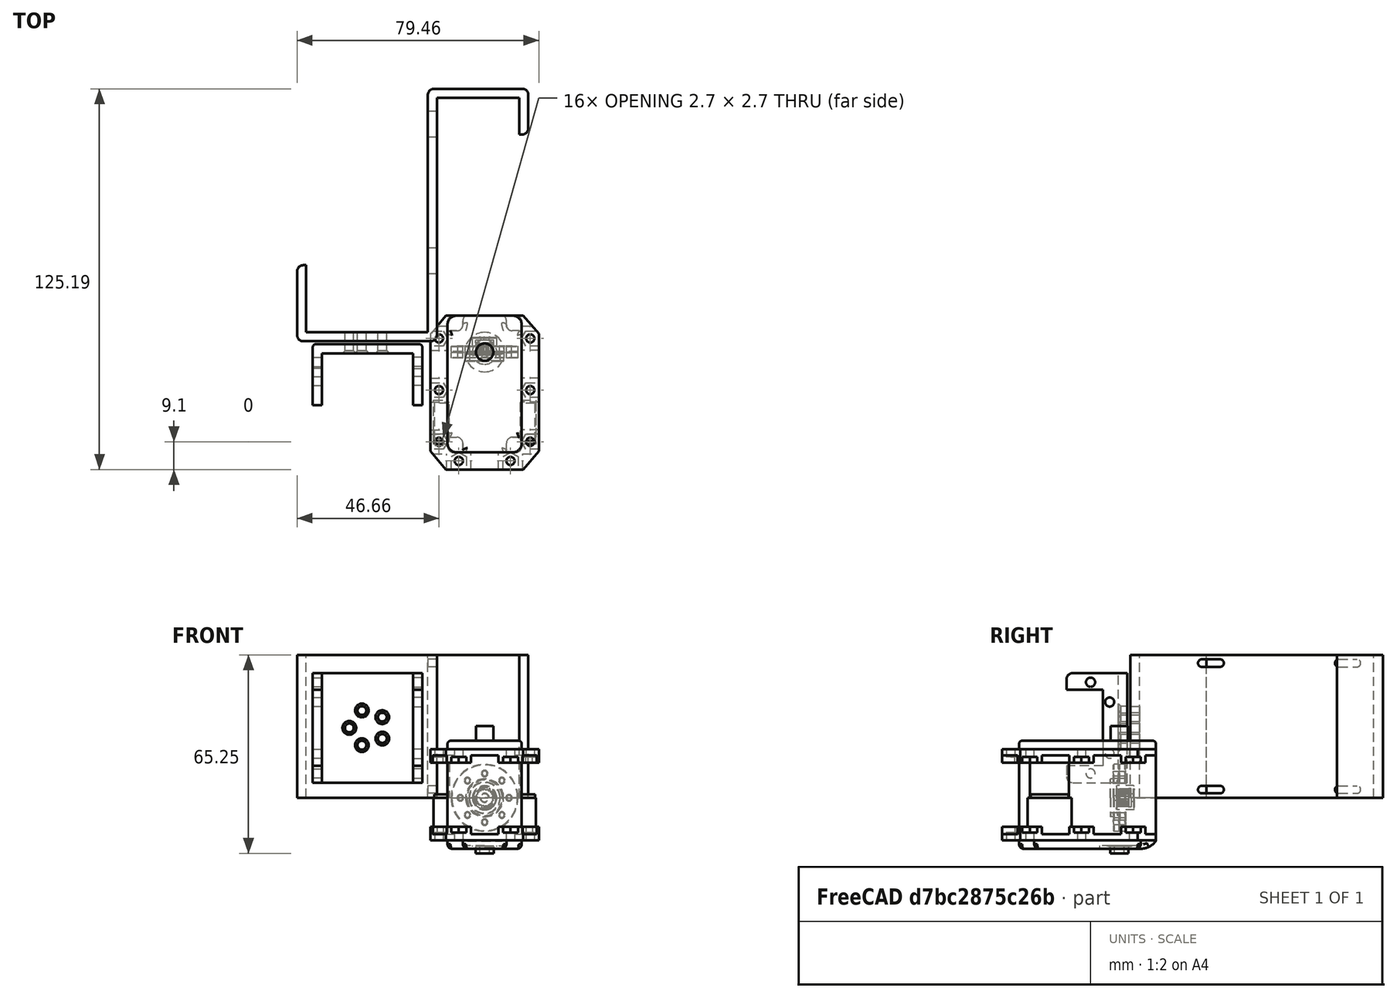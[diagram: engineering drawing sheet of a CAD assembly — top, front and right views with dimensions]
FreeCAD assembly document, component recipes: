
FREECAD ASSEMBLY — COMPONENT RECIPES ("test2")

This assembly document has 7 components, labeled P0..P6 below (a component is one placed body or linked part). 4 of them carry a construction recipe — the FreeCAD feature program that regenerates the part from scratch, quoted from this document or its linked companion documents; the rest are supplied as boundary geometry only. No exploded tour is included for this assembly.
COMPONENT P0 — geometry summary ("ASM0001_ASM"; no construction recipe available for this part):
  bounding box: 50.9 x 40.0 x 33.5 mm
  tessellated surface: 109,530 triangles
  volume: 42792 mm^3 (63% of its bounding box)
COMPONENT P1 — geometry summary ("ASM0001_ASM001"; no construction recipe available for this part):
  bounding box: 50.9 x 40.0 x 33.5 mm
  tessellated surface: 109,530 triangles
  volume: 42792 mm^3 (63% of its bounding box)
COMPONENT P2 — recipe-attached ("Body003", modeled in this document).
Construction recipe (the document's own serialized feature program — sketch geometry with constraints, then the solid features built on it; lengths are millimeters unless a unit is written):

FEATURE [PartDesign::ShapeBinder] CopyPart__Feature
  TraceSupport = false
FEATURE [Sketcher::SketchObject] Sketch002
  ArcFitTolerance = 1e-06
  AttachmentSupport = -> [CopyPart__Feature]
  ExternalTypes = [0]
  FullyConstrained = true
  MakeInternals = false
  MapMode = 5
  Placement = pos=(0,-38.6,0) rot=(1,0,0;1.5708rad)
  _ExternalGeoVersion = 1
  sketch-geometry (5):
    g0: LineSegment StartX=-18 StartY=-15 StartZ=0 EndX=18 EndY=-15 EndZ=0
    g1: LineSegment StartX=18 StartY=-15 StartZ=0 EndX=18 EndY=15 EndZ=0
    g2: LineSegment StartX=18 StartY=15 StartZ=0 EndX=-18 EndY=15 EndZ=0
    g3: LineSegment StartX=-18 StartY=15 StartZ=0 EndX=-18 EndY=-15 EndZ=0
    g4: GeomPoint [constr] X=0 Y=0 Z=0
  constraints (12):
    c: Coincident(g0,g1)
    c: Coincident(g1,g2)
    c: Coincident(g2,g3)
    c: Coincident(g3,g0)
    c: Horizontal(g0)
    c: Horizontal(g2)
    c: Vertical(g1)
    c: Vertical(g3)
    c: Symmetric(g2,g0,g4)
    c: Distance(g1,g3) = 36
    c: Distance(g0,g2) = 30
    c: Coincident(g4,g-1)
FEATURE [PartDesign::Pad] Pad001
  Direction = (0,-1,2e-16)
  Length = 3
  Length2 = 10
  Profile = -> Sketch002
  ReferenceAxis = -> Sketch002 [N_Axis]
  Refine = true
  SideType = 0
  Suppressed = false
  Type = 0
  Type2 = 0
FEATURE [Sketcher::SketchObject] Sketch003
  ArcFitTolerance = 1e-06
  AttachmentSupport = -> [Pad001]
  ExternalTypes = [0]
  FullyConstrained = true
  MakeInternals = false
  MapMode = 5
  Placement = pos=(0,3.3e-15,15) rot=(0,0,1;0rad)
  _ExternalGeoVersion = 1
  sketch-geometry (12):
    g0: LineSegment StartX=-18 StartY=-21.6 StartZ=0 EndX=-12.5 EndY=-21.6 EndZ=0
    g1: LineSegment StartX=-12.5 StartY=-21.6 StartZ=0 EndX=-12.5 EndY=-33.6 EndZ=0
    g2: LineSegment StartX=-12.5 StartY=-33.6 StartZ=0 EndX=12.5 EndY=-33.6 EndZ=0
    g3: LineSegment StartX=12.5 StartY=-33.6 StartZ=0 EndX=12.5 EndY=-21.6 EndZ=0
    g4: LineSegment StartX=12.5 StartY=-21.6 StartZ=0 EndX=18 EndY=-21.6 EndZ=0
    g5: LineSegment StartX=18 StartY=-21.6 StartZ=0 EndX=18 EndY=-41.6 EndZ=0
    g6: LineSegment StartX=18 StartY=-41.6 StartZ=0 EndX=-18 EndY=-41.6 EndZ=0
    g7: LineSegment StartX=-18 StartY=-41.6 StartZ=0 EndX=-18 EndY=-21.6 EndZ=0
    g8: Circle CenterX=-15 CenterY=-29.5 CenterZ=0 NormalX=0 NormalY=0 NormalZ=1 AngleXU=0 Radius=1.5
    g9: Circle CenterX=-8.5 CenterY=-35.8 CenterZ=0 NormalX=0 NormalY=0 NormalZ=1 AngleXU=0 Radius=1.5
    g10: Circle CenterX=8.5 CenterY=-35.8 CenterZ=0 NormalX=0 NormalY=0 NormalZ=1 AngleXU=0 Radius=1.5
    g11: Circle CenterX=15 CenterY=-29.5 CenterZ=0 NormalX=0 NormalY=0 NormalZ=1 AngleXU=0 Radius=1.5
  constraints (36):
    c: Horizontal(g0)
    c: Coincident(g0,g1)
    c: Vertical(g1)
    c: Coincident(g1,g2)
    c: Horizontal(g2)
    c: Coincident(g2,g3)
    c: Vertical(g3)
    c: Coincident(g3,g4)
    c: Horizontal(g4)
    c: Coincident(g4,g5)
    c: Vertical(g5)
    c: Coincident(g5,g6)
    c: Horizontal(g6)
    c: Coincident(g6,g7)
    c: Coincident(g7,g0)
    c: Vertical(g7)
    c: DistanceX(g6,g6) = 36
    c: DistanceY(g7,g7) = 20
    c: Distance(g3,g1) = 25
    c: Equal(g0,g4)
    c: Equal(g3,g1)
    c: Distance(g-1,g6) = 41.6
    c: Distance(g-2,g7) = 18
    c: Distance(g6,g2) = 8
    c: Diameter(g8) = 3
    c: Equal(g8,g9)
    c: Equal(g9,g10)
    c: Equal(g10,g11)
    c: Distance(g8,g7) = 3
    c: Distance(g9,g6) = 5.8
    c: Distance(g9,g7) = 9.5
    c: Distance(g10,g5) = 9.5
    c: Distance(g10,g6) = 5.8
    c: Distance(g11,g5) = 3
    c: Distance(g8,g0) = 7.9
    c: Distance(g11,g4) = 7.9
FEATURE [PartDesign::Pad] Pad002
  BaseFeature = -> Pad001
  Direction = (0,0,1)
  Length = 3
  Length2 = 10
  Profile = -> Sketch003
  ReferenceAxis = -> Sketch003 [N_Axis]
  Refine = true
  SideType = 0
  Suppressed = false
  Type = 0
  Type2 = 0
FEATURE [PartDesign::Mirrored] Mirrored
  BaseFeature = -> Pad002
  MirrorPlane = -> XY_Plane001
  Originals = -> [Pad002]
  Refine = true
  Suppressed = false
  TransformMode = 0
FEATURE [PartDesign::Fillet] Fillet001
  Base = -> Mirrored [Edge60,Edge47,Edge36,Edge27]
  BaseFeature = -> Mirrored
  Radius = 2
  Refine = true
  SupportTransform = false
  Suppressed = false
  UseAllEdges = false
FEATURE [PartDesign::Fillet] Fillet002
  Base = -> Fillet001 [Edge51,Edge56]
  BaseFeature = -> Fillet001
  Radius = 1
  Refine = true
  SupportTransform = false
  Suppressed = false
  UseAllEdges = false
FEATURE [Sketcher::SketchObject] Sketch004
  ArcFitTolerance = 1e-06
  AttachmentSupport = -> [Fillet002]
  ExternalTypes = [0]
  FullyConstrained = true
  MakeInternals = false
  MapMode = 5
  Placement = pos=(0,-38.6,0) rot=(0,0.707107,0.707107;3.14159rad)
  _ExternalGeoVersion = 1
  sketch-geometry (1):
    g0: Circle CenterX=0 CenterY=6 CenterZ=0 NormalX=0 NormalY=0 NormalZ=1 AngleXU=0 Radius=1.25
  constraints (3):
    c: Diameter(g0) = 2.5
    c: PointOnObject(g0,g-2)
    c: Distance(g0,g-1) = 6
FEATURE [PartDesign::Hole] Hole
  BaseFeature = -> Fillet002
  BaseProfileType = 7
  CustomThreadClearance = 0
  Depth = 5
  DepthType = 0
  Diameter = 2.9
  DrillForDepth = false
  DrillPoint = 1
  DrillPointAngle = 118
  HoleCutCountersinkAngle = 90
  HoleCutCustomValues = false
  HoleCutDepth = 2.65
  HoleCutDiameter = 5.3
  HoleCutType = 7
  ModelThread = false
  Profile = -> Sketch004
  Refine = true
  Suppressed = false
  Tapered = false
  TaperedAngle = 90
  ThreadClass = 0
  ThreadDepth = 5
  ThreadDepthType = 0
  ThreadDiameter = 2.5
  ThreadDirection = 0
  ThreadFit = 0
  ThreadSize = 8
  ThreadType = 1
  Threaded = false
  UseCustomThreadClearance = false
FEATURE [PartDesign::PolarPattern] PolarPattern
  Angle = 360
  Axis = -> Sketch004 [N_Axis]
  BaseFeature = -> Hole
  Mode = 0
  Occurrences = 5
  Offset = 120
  Originals = -> [Hole]
  Refine = true
  SpacingPattern = [0]
  Spacings = [-1,-1,-1,-1]
  Suppressed = false
  TransformMode = 0
FEATURE [PartDesign::Body] Body001
  AllowCompound = true
  Group = -> [CopyPart__Feature,Sketch002,Pad001,Sketch003,Pad002,Mirrored,Fillet001,Fillet002,Sketch004,Hole,PolarPattern]
  Origin = -> Origin002
  Placement = pos=(-38.5,-39,23) rot=(0.707107,0,-0.707107;3.14159rad)
  Tip = -> PolarPattern
COMPONENT P3 — recipe-attached ("Body004", modeled in this document).
Construction recipe (the document's own serialized feature program — sketch geometry with constraints, then the solid features built on it; lengths are millimeters unless a unit is written):

FEATURE [Sketcher::SketchObject] Sketch
  ArcFitTolerance = 1e-06
  AttachmentSupport = -> [Origin]
  ExternalTypes = [0]
  FullyConstrained = true
  MakeInternals = false
  MapMode = 5
  _ExternalGeoVersion = 1
  sketch-geometry (12):
    g0: LineSegment StartX=-18.66 StartY=86.59 StartZ=0 EndX=-18.66 EndY=6.59 EndZ=0
    g1: LineSegment StartX=-61.66 StartY=3.59 StartZ=0 EndX=-61.66 EndY=28.59 EndZ=0
    g2: LineSegment StartX=-61.66 StartY=28.59 StartZ=0 EndX=-58.66 EndY=28.59 EndZ=0
    g3: LineSegment StartX=-58.66 StartY=28.59 StartZ=0 EndX=-58.66 EndY=6.59 EndZ=0
    g4: LineSegment StartX=-58.66 StartY=6.59 StartZ=0 EndX=-18.66 EndY=6.59 EndZ=0
    g5: LineSegment StartX=-15.66 StartY=83.59 StartZ=0 EndX=-15.66 EndY=3.59 EndZ=0
    g6: LineSegment StartX=-15.66 StartY=3.59 StartZ=0 EndX=-61.66 EndY=3.59 EndZ=0
    g7: LineSegment StartX=-15.66 StartY=83.59 StartZ=0 EndX=11.34 EndY=83.59 EndZ=0
    g8: LineSegment StartX=11.34 StartY=83.59 StartZ=0 EndX=11.34 EndY=71.59 EndZ=0
    g9: LineSegment StartX=11.34 StartY=71.59 StartZ=0 EndX=14.34 EndY=71.59 EndZ=0
    g10: LineSegment StartX=14.34 StartY=71.59 StartZ=0 EndX=14.34 EndY=86.59 EndZ=0
    g11: LineSegment StartX=14.34 StartY=86.59 StartZ=0 EndX=-18.66 EndY=86.59 EndZ=0
  constraints (36):
    c: Coincident(g1,g2)
    c: Coincident(g2,g3)
    c: Coincident(g3,g4)
    c: Coincident(g4,g0)
    c: Distance(g2,g2) = 3
    c: Vertical(g5)
    c: Coincident(g5,g6)
    c: Coincident(g6,g1)
    c: Perpendicular(g4,g3)
    c: Horizontal(g4)
    c: Horizontal(g6)
    c: Vertical(g1)
    c: Vertical(g0)
    c: Horizontal(g2)
    c: Distance(g6,g4) = 3
    c: Distance(g5,g0) = 3
    c: DistanceX(g4,g4) = 40
    c: Distance(g1,g1) = 25
    c: Distance(g-2,g5) = 15.66
    c: Distance(g-1,g6) = 3.59
    c: DistanceY(g0,g0) = 80
    c: Coincident(g5,g7)
    c: Horizontal(g7)
    c: Coincident(g7,g8)
    c: Vertical(g8)
    c: Coincident(g8,g9)
    c: Horizontal(g9)
    c: Coincident(g9,g10)
    c: Vertical(g10)
    c: Coincident(g10,g11)
    c: Coincident(g11,g0)
    c: Equal(g9,g2)
    c: Horizontal(g11)
    c: Distance(g11,g7) = 3
    c: Distance(g7,g7) = 27
    c: DistanceY(g10,g10) = 15
FEATURE [PartDesign::Pad] Pad
  Direction = (0,0,1)
  Length = 47
  Length2 = 10
  Profile = -> Sketch
  ReferenceAxis = -> Sketch [N_Axis]
  Refine = true
  SideType = 0
  Suppressed = false
  Type = 0
  Type2 = 0
FEATURE [Sketcher::SketchObject] Sketch001
  ArcFitTolerance = 1e-06
  ExternalTypes = [0]
  FullyConstrained = true
  MakeInternals = false
  MapMode = 5
  Placement = pos=(-15.66,0,0) rot=(0.57735,0.57735,0.57735;2.0944rad)
  _ExternalGeoVersion = 1
  sketch-geometry (8):
    g0: ArcOfCircle CenterX=72.09 CenterY=2.7 CenterZ=0 NormalX=0 NormalY=0 NormalZ=1 AngleXU=0 Radius=1.25 StartAngle=1.5708 EndAngle=4.71239
    g1: ArcOfCircle CenterX=78.09 CenterY=2.7 CenterZ=0 NormalX=0 NormalY=0 NormalZ=1 AngleXU=0 Radius=1.25 StartAngle=4.71239 EndAngle=7.85398
    g2: LineSegment StartX=72.09 StartY=3.95 StartZ=0 EndX=78.09 EndY=3.95 EndZ=0
    g3: LineSegment StartX=72.09 StartY=1.45 StartZ=0 EndX=78.09 EndY=1.45 EndZ=0
    g4: ArcOfCircle CenterX=27.09 CenterY=2.7 CenterZ=0 NormalX=0 NormalY=0 NormalZ=1 AngleXU=0 Radius=1.25 StartAngle=1.5708 EndAngle=4.71239
    g5: ArcOfCircle CenterX=33.09 CenterY=2.7 CenterZ=0 NormalX=0 NormalY=0 NormalZ=1 AngleXU=0 Radius=1.25 StartAngle=4.71239 EndAngle=7.85398
    g6: LineSegment StartX=27.09 StartY=3.95 StartZ=0 EndX=33.09 EndY=3.95 EndZ=0
    g7: LineSegment StartX=27.09 StartY=1.45 StartZ=0 EndX=33.09 EndY=1.45 EndZ=0
  constraints (20):
    c: Tangent(g0,g2) = 1.5708
    c: Tangent(g0,g3) = -1.5708
    c: Tangent(g1,g2) = 1.5708
    c: Tangent(g1,g3) = -1.5708
    c: Equal(g0,g1)
    c: Distance(g0,g1) = 6
    c: Radius(g0) = 1.25
    c: Horizontal(g2)
    c: Distance(g1,g-1) = 2.7
    c: DistanceX(g-1,g1) = 78.09
    c: Tangent(g4,g6) = 1.5708
    c: Tangent(g4,g7) = -1.5708
    c: Tangent(g5,g6) = 1.5708
    c: Tangent(g5,g7) = -1.5708
    c: Equal(g4,g5)
    c: Distance(g4,g5) = 6
    c: Radius(g4) = 1.25
    c: Horizontal(g6)
    c: DistanceX(g5,g1) = 45
    c: Distance(g5,g-1) = 2.7
FEATURE [PartDesign::Fillet] Fillet
  Base = -> Pad [Edge26,Edge29,Edge32,Edge8,Edge11,Edge14]
  BaseFeature = -> Pad
  Radius = 2
  Refine = true
  SupportTransform = false
  Suppressed = false
  UseAllEdges = false
FEATURE [PartDesign::Pocket] Pocket
  BaseFeature = -> Fillet
  Direction = (-1,0,0)
  Length = 5
  Length2 = 5
  Profile = -> Sketch001
  ReferenceAxis = -> Sketch001 [N_Axis]
  Refine = true
  SideType = 0
  Suppressed = false
  Type = 0
  Type2 = 0
FEATURE [PartDesign::LinearPattern] LinearPattern
  BaseFeature = -> Pocket
  Direction = -> Sketch001 [V_Axis]
  Direction2 = -> Sketch001 [V_Axis]
  Length = 41.6
  Length2 = 100
  Mode = 0
  Mode2 = 0
  Occurrences = 2
  Occurrences2 = 1
  Offset = 41.6
  Offset2 = 100
  Originals = -> [Pocket]
  Refine = true
  Reversed2 = false
  SpacingPattern = [0]
  SpacingPattern2 = [0]
  Spacings = [-1]
  Suppressed = false
  TransformMode = 0
FEATURE [Sketcher::SketchObject] Sketch005
  ArcFitTolerance = 1e-06
  AttachmentSupport = -> [LinearPattern]
  ExternalTypes = [0]
  FullyConstrained = true
  MakeInternals = false
  Placement = pos=(0,3.59,0) rot=(1,0,0;1.5708rad)
  _ExternalGeoVersion = 1
  sketch-geometry (5):
    g0: Circle CenterX=-40.37 CenterY=17.3 CenterZ=0 NormalX=0 NormalY=0 NormalZ=1 AngleXU=0 Radius=1.25
    g1: Circle CenterX=-44.5 CenterY=23 CenterZ=0 NormalX=0 NormalY=0 NormalZ=1 AngleXU=0 Radius=1.25
    g2: Circle CenterX=-40.36 CenterY=28.7 CenterZ=0 NormalX=0 NormalY=0 NormalZ=1 AngleXU=0 Radius=1.25
    g3: Circle CenterX=-33.65 CenterY=26.55 CenterZ=0 NormalX=0 NormalY=0 NormalZ=1 AngleXU=0 Radius=1.25
    g4: Circle CenterX=-33.65 CenterY=19.5 CenterZ=0 NormalX=0 NormalY=0 NormalZ=1 AngleXU=0 Radius=1.25
  constraints (15):
    c: Diameter(g0) = 2.5
    c: Distance(g0,g-1) = 17.3
    c: Distance(g0,g-2) = 40.37
    c: Equal(g1,g0)
    c: Distance(g1,g-1) = 23
    c: DistanceX(g1,g-1) = 44.5
    c: Equal(g2,g1)
    c: Equal(g3,g2)
    c: Equal(g4,g3)
    c: Distance(g2,g-1) = 28.7
    c: Distance(g2,g-2) = 40.36
    c: Distance(g3,g-2) = 33.65
    c: Distance(g3,g-1) = 26.55
    c: Distance(g4,g-2) = 33.65
    c: DistanceY(g-1,g4) = 19.5
FEATURE [PartDesign::Hole] Hole001
  BaseFeature = -> LinearPattern
  BaseProfileType = 7
  CustomThreadClearance = 0
  Depth = 5
  DepthType = 0
  Diameter = 2.9
  DrillForDepth = false
  DrillPoint = 1
  DrillPointAngle = 118
  HoleCutCountersinkAngle = 90
  HoleCutCustomValues = false
  HoleCutDepth = 0
  HoleCutDiameter = 5.3
  HoleCutType = 0
  ModelThread = false
  Profile = -> Sketch005
  Refine = true
  Suppressed = false
  Tapered = false
  TaperedAngle = 90
  ThreadClass = 0
  ThreadDepth = 5
  ThreadDepthType = 0
  ThreadDiameter = 2.5
  ThreadDirection = 0
  ThreadFit = 0
  ThreadSize = 8
  ThreadType = 1
  Threaded = false
  UseCustomThreadClearance = false
FEATURE [PartDesign::Body] Body
  AllowCompound = true
  Group = -> [Sketch,Pad,Fillet,Sketch001,Pocket,LinearPattern,Sketch005,Hole001]
  Origin = -> Origin
  Tip = -> Hole001
COMPONENT P4 — same part as P2; its construction recipe is shown at P2.
COMPONENT P5 — same part as P3; its construction recipe is shown at P3.
COMPONENT P6 — geometry summary ("mx001"; no construction recipe available for this part):
  bounding box: 50.6 x 43.3 x 35.6 mm
  tessellated surface: 47,532 triangles
  volume: 44571 mm^3 (57% of its bounding box)
  symmetry: mirror-symmetric across its z mid-plane
PROVENANCE & LICENSES
A FreeCAD (.FCStd) document from a public repository crawl; recipes are the document's own serialized feature recipes (and, for linked parts, companion documents' recipes).
License: mit.
